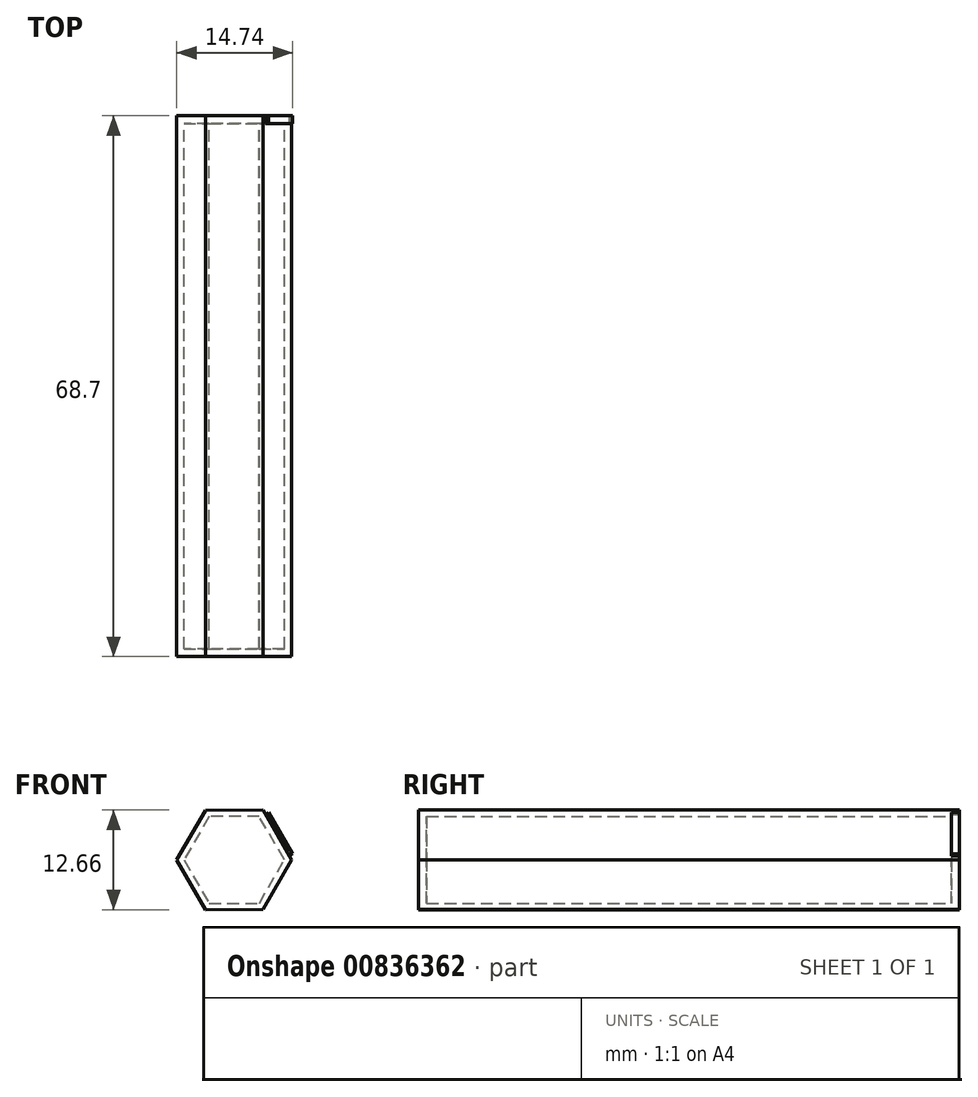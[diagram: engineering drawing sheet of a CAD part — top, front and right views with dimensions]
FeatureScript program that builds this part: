
annotation { "Feature Type Name" : "Feature", "Feature Type Description" : "" }
export const myFeature = defineFeature(function(context is Context, id is Id, definition is map)
    precondition{}
    {
        {
            var Q0;
            Q0=qCreatedBy(makeId("Front.planeOp"),FACE);
            var sketch = newSketch(context, id + "F0", { "sketchPlane" : qUnion([Q0])});
            skLineSegment(sketch, "E0.0", {"start": v(3.64, 6.33) * mm, "end": v(7.3, 0.02) * mm});
            skLineSegment(sketch, "E0.1", {"start": v(7.3, 0.02) * mm, "end": v(3.66, -6.31) * mm});
            skLineSegment(sketch, "E0.2", {"start": v(3.66, -6.31) * mm, "end": v(-3.64, -6.33) * mm});
            skLineSegment(sketch, "E0.3", {"start": v(-3.64, -6.33) * mm, "end": v(-7.3, -0.02) * mm});
            skLineSegment(sketch, "E0.4", {"start": v(-7.3, -0.02) * mm, "end": v(-3.66, 6.31) * mm});
            skLineSegment(sketch, "E0.5", {"start": v(-3.66, 6.31) * mm, "end": v(3.64, 6.33) * mm});
            skPoint(sketch, "E0.0.midPoint", {"position": v(5.47, 3.17) * mm});
            skSolve(sketch);
        }
        {
            var Q0;
            Q0=makeQuery(id+"F0.imprint","IMPRINT",FACE,{"disambiguationData":[TD([[makeQuery(id+"F0.imprint","IMPRINT",EDGE,{"derivedFrom":sQuery(id+"F0.wireOp",EDGE,"E0.0")}),-1.0]])]});
            extrude(context, id + "F1", {"entities" : qUnion([Q0]), "depth" : 69.5 * mm, "offsetDistance" : 25 * mm});
        }
        {
            var Q0;
            Q0=makeQuery(id+"F1.opExtrude","CAP_FACE",FACE,{"disambiguationData":[OSD([sQuery(id+"F0.wireOp",EDGE,"E0.0"),sQuery(id+"F0.wireOp",EDGE,"E0.1"),sQuery(id+"F0.wireOp",EDGE,"E0.2"),sQuery(id+"F0.wireOp",EDGE,"E0.3"),sQuery(id+"F0.wireOp",EDGE,"E0.4"),sQuery(id+"F0.wireOp",EDGE,"E0.5")])],"isStart":true});
            shell(context, id + "F2", {"entities" : qUnion([Q0]), "thickness" : 0.8 * mm});
        }
        {
            var Q0;
            Q0=makeQuery(id+"F1.opExtrude","CAP_FACE",FACE,{"disambiguationData":[OSD([sQuery(id+"F0.wireOp",EDGE,"E0.0"),sQuery(id+"F0.wireOp",EDGE,"E0.1"),sQuery(id+"F0.wireOp",EDGE,"E0.2"),sQuery(id+"F0.wireOp",EDGE,"E0.3"),sQuery(id+"F0.wireOp",EDGE,"E0.4"),sQuery(id+"F0.wireOp",EDGE,"E0.5")])],"isStart":false});
            extrude(context, id + "F3", {"entities" : qUnion([Q0]), "operationType" : NewBodyOperationType.REMOVE, "oppositeDirection" : true, "depth" : 0.8 * mm, "offsetDistance" : 25 * mm});
        }
        {
            var Q0;
            Q0=makeQuery(id+"F3.boolean.opBoolean","COPY",FACE,{"derivedFrom":makeQuery(id+"F3.opExtrude","CAP_FACE",FACE,{"disambiguationData":[OSD([sQuery(id+"F0.wireOp",EDGE,"E0.0"),sQuery(id+"F0.wireOp",EDGE,"E0.1"),sQuery(id+"F0.wireOp",EDGE,"E0.2"),sQuery(id+"F0.wireOp",EDGE,"E0.3"),sQuery(id+"F0.wireOp",EDGE,"E0.4"),sQuery(id+"F0.wireOp",EDGE,"E0.5")])],"isStart":false})});
            var sketch = newSketch(context, id + "F4", { "sketchPlane" : qUnion([Q0])});
            skLineSegment(sketch, "E1", {"start": v(3.18, 5.53) * mm, "end": v(6.38, 0.01) * mm});
            skLineSegment(sketch, "E2", {"start": v(7.3, 0.02) * mm, "end": v(3.64, 6.33) * mm});
            skLineSegment(sketch, "E3", {"start": v(-7.3, -0.02) * mm, "end": v(-3.64, -6.33) * mm});
            skLineSegment(sketch, "E4", {"start": v(-3.18, -5.53) * mm, "end": v(-6.38, -0.01) * mm});
            skLineSegment(sketch, "E5", {"start": v(3.64, 6.33) * mm, "end": v(5.47, 3.17) * mm});
            skLineSegment(sketch, "E6", {"start": v(5.47, 3.17) * mm, "end": v(-5.47, -3.17) * mm});
            skLineSegment(sketch, "E7", {"start": v(-4.78, -2.77) * mm, "end": v(4.78, 2.77) * mm});
            skSolve(sketch);
        }
        {
            var Q0;
            {var subQ3=sQuery(id+"F4.wireOp",EDGE,"E7");Q0=makeQuery(id+"F4.imprint","IMPRINT",FACE,{"disambiguationData":[TD([[makeQuery(id+"F4.imprint","IMPRINT",EDGE,{"derivedFrom":subQ3}),1.0]])]});}
            var sketch = newSketch(context, id + "F5", { "sketchPlane" : qUnion([Q0])});
            skLineSegment(sketch, "E8", {"start": v(-3.2, 5.52) * mm, "end": v(3.18, 5.53) * mm});
            skLineSegment(sketch, "E9", {"start": v(3.18, 5.53) * mm, "end": v(6.38, 0.01) * mm});
            skLineSegment(sketch, "E10", {"start": v(6.38, 0.01) * mm, "end": v(3.2, -5.51) * mm});
            skLineSegment(sketch, "E11", {"start": v(3.2, -5.51) * mm, "end": v(-3.18, -5.53) * mm});
            skLineSegment(sketch, "E12", {"start": v(-3.18, -5.53) * mm, "end": v(-6.38, -0.01) * mm});
            skLineSegment(sketch, "E13", {"start": v(-6.38, -0.01) * mm, "end": v(-3.2, 5.52) * mm});
            skLineSegment(sketch, "E14", {"start": v(-3, 5.52) * mm, "end": v(-3, 5.02) * mm});
            skLineSegment(sketch, "E15", {"start": v(2.3, 5.53) * mm, "end": v(2.3, 5.03) * mm});
            skLineSegment(sketch, "E16", {"start": v(3.7, 4.62) * mm, "end": v(3.27, 4.37) * mm});
            skLineSegment(sketch, "E17", {"start": v(5.9, 0.85) * mm, "end": v(5.46, 0.6) * mm});
            skLineSegment(sketch, "E18", {"start": v(5.86, -0.9) * mm, "end": v(5.42, -0.64) * mm});
            skLineSegment(sketch, "E19", {"start": v(3.7, -4.64) * mm, "end": v(3.27, -4.4) * mm});
            skLineSegment(sketch, "E20", {"start": v(2.49, -5.52) * mm, "end": v(2.49, -5.02) * mm});
            skLineSegment(sketch, "E21", {"start": v(-2.37, -5.53) * mm, "end": v(-2.37, -5.03) * mm});
            skLineSegment(sketch, "E22", {"start": v(-3.8, -4.47) * mm, "end": v(-3.36, -4.22) * mm});
            skLineSegment(sketch, "E23", {"start": v(-5.9, -0.82) * mm, "end": v(-5.47, -0.57) * mm});
            skLineSegment(sketch, "E24", {"start": v(-5.88, 0.85) * mm, "end": v(-5.45, 0.6) * mm});
            skLineSegment(sketch, "E25", {"start": v(-3.8, 4.48) * mm, "end": v(-3.36, 4.23) * mm});
            skLineSegment(sketch, "E26", {"start": v(-3, 5.02) * mm, "end": v(2.3, 5.03) * mm});
            skLineSegment(sketch, "E27", {"start": v(3.27, 4.37) * mm, "end": v(5.46, 0.6) * mm});
            skLineSegment(sketch, "E28", {"start": v(5.42, -0.64) * mm, "end": v(3.27, -4.4) * mm});
            skLineSegment(sketch, "E29", {"start": v(2.49, -5.02) * mm, "end": v(-2.37, -5.03) * mm});
            skLineSegment(sketch, "E30", {"start": v(-3.36, -4.22) * mm, "end": v(-5.47, -0.57) * mm});
            skLineSegment(sketch, "E31", {"start": v(-5.45, 0.6) * mm, "end": v(-2.91, 5.02) * mm});
            skLineSegment(sketch, "E32", {"start": v(2.3, 5.03) * mm, "end": v(3.2, 5.03) * mm});
            skLineSegment(sketch, "E33", {"start": v(3.27, 4.37) * mm, "end": v(2.89, 5.03) * mm});
            skLineSegment(sketch, "E34", {"start": v(5.42, -0.64) * mm, "end": v(5.94, 0.27) * mm});
            skLineSegment(sketch, "E35", {"start": v(5.46, 0.6) * mm, "end": v(5.8, 0) * mm});
            skLineSegment(sketch, "E36", {"start": v(3.27, -4.4) * mm, "end": v(2.83, -5.16) * mm});
            skLineSegment(sketch, "E37", {"start": v(2.49, -5.02) * mm, "end": v(2.91, -5.02) * mm});
            skLineSegment(sketch, "E38", {"start": v(-2.37, -5.03) * mm, "end": v(-3.17, -5.03) * mm});
            skLineSegment(sketch, "E39", {"start": v(-3.36, -4.22) * mm, "end": v(-2.89, -5.03) * mm});
            skLineSegment(sketch, "E40", {"start": v(-5.47, -0.57) * mm, "end": v(-5.94, 0.23) * mm});
            skLineSegment(sketch, "E41", {"start": v(-5.45, 0.6) * mm, "end": v(-5.8, -0.01) * mm});
            skSolve(sketch);
        }
        {
            var Q0;
            Q0=qSketchRegion(id+"F5",true);
            extrude(context, id + "F6", {"entities" : qUnion([Q0]), "operationType" : NewBodyOperationType.ADD, "oppositeDirection" : true, "depth" : 1 * mm, "offsetDistance" : 25 * mm});
        }
        {
            var Q0;
            Q0=makeQuery(id+"F1.opExtrude","CAP_FACE",FACE,{"disambiguationData":[OSD([sQuery(id+"F0.wireOp",EDGE,"E0.0"),sQuery(id+"F0.wireOp",EDGE,"E0.1"),sQuery(id+"F0.wireOp",EDGE,"E0.2"),sQuery(id+"F0.wireOp",EDGE,"E0.3"),sQuery(id+"F0.wireOp",EDGE,"E0.4"),sQuery(id+"F0.wireOp",EDGE,"E0.5")])],"isStart":true});
            var sketch = newSketch(context, id + "F7", { "sketchPlane" : qUnion([Q0])});
            skLineSegment(sketch, "E42.0", {"start": v(3.66, 6.31) * mm, "end": v(7.3, -0.02) * mm});
            skLineSegment(sketch, "E42.1", {"start": v(7.3, -0.02) * mm, "end": v(3.64, -6.33) * mm});
            skLineSegment(sketch, "E42.2", {"start": v(3.64, -6.33) * mm, "end": v(-3.66, -6.31) * mm});
            skLineSegment(sketch, "E42.3", {"start": v(-3.66, -6.31) * mm, "end": v(-7.3, 0.02) * mm});
            skLineSegment(sketch, "E42.4", {"start": v(-7.3, 0.02) * mm, "end": v(-3.64, 6.33) * mm});
            skLineSegment(sketch, "E42.5", {"start": v(-3.64, 6.33) * mm, "end": v(3.66, 6.31) * mm});
            skPoint(sketch, "E42.0.midPoint", {"position": v(5.48, 3.15) * mm});
            skLineSegment(sketch, "E43", {"start": v(-3.3, 6.33) * mm, "end": v(-3.3, 6.83) * mm});
            skLineSegment(sketch, "E44", {"start": v(3.41, 6.31) * mm, "end": v(3.41, 6.81) * mm});
            skLineSegment(sketch, "E45", {"start": v(3.96, 5.8) * mm, "end": v(4.4, 6.05) * mm});
            skLineSegment(sketch, "E46", {"start": v(7, 0.5) * mm, "end": v(7.44, 0.74) * mm});
            skLineSegment(sketch, "E47", {"start": v(7, -0.55) * mm, "end": v(7.42, -0.8) * mm});
            skLineSegment(sketch, "E48", {"start": v(4.18, -5.4) * mm, "end": v(4.61, -5.65) * mm});
            skLineSegment(sketch, "E49", {"start": v(3, -6.33) * mm, "end": v(3, -6.83) * mm});
            skLineSegment(sketch, "E50", {"start": v(-3.12, -6.32) * mm, "end": v(-3.12, -6.82) * mm});
            skLineSegment(sketch, "E51", {"start": v(-3.99, -5.75) * mm, "end": v(-4.42, -6) * mm});
            skLineSegment(sketch, "E52", {"start": v(-6.67, -1.09) * mm, "end": v(-7.1, -1.33) * mm});
            skLineSegment(sketch, "E53", {"start": v(-7.01, 0.51) * mm, "end": v(-7.44, 0.76) * mm});
            skLineSegment(sketch, "E54", {"start": v(-3.96, 5.77) * mm, "end": v(-4.4, 6.02) * mm});
            skLineSegment(sketch, "E55", {"start": v(-3.3, 6.83) * mm, "end": v(3.41, 6.81) * mm});
            skLineSegment(sketch, "E56", {"start": v(4.4, 6.05) * mm, "end": v(8.5, -1.1) * mm});
            skLineSegment(sketch, "E57", {"start": v(7.42, -0.8) * mm, "end": v(3.8, -7.03) * mm});
            skLineSegment(sketch, "E58", {"start": v(3, -6.83) * mm, "end": v(-5.02, -6.81) * mm});
            skLineSegment(sketch, "E59", {"start": v(-4.42, -6) * mm, "end": v(-8.1, 0.4) * mm});
            skLineSegment(sketch, "E60", {"start": v(-7.44, 0.76) * mm, "end": v(-3.69, 7.24) * mm});
            skLineSegment(sketch, "E61", {"start": v(-3.3, 6.83) * mm, "end": v(-3.92, 6.83) * mm});
            skLineSegment(sketch, "E62", {"start": v(4.4, 6.05) * mm, "end": v(3.82, 7.04) * mm});
            skLineSegment(sketch, "E63", {"start": v(3.41, 6.81) * mm, "end": v(3.95, 6.81) * mm});
            skLineSegment(sketch, "E64", {"start": v(7.42, -0.8) * mm, "end": v(7.88, -0.02) * mm});
            skLineSegment(sketch, "E65", {"start": v(3, -6.83) * mm, "end": v(3.92, -6.83) * mm});
            skLineSegment(sketch, "E66", {"start": v(-4.42, -6) * mm, "end": v(-3.95, -6.81) * mm});
            skLineSegment(sketch, "E67", {"start": v(-7.44, 0.76) * mm, "end": v(-7.88, 0.02) * mm});
            skSolve(sketch);
        }
        {
            var Q0;
            Q0=qSketchRegion(id+"F7",true);
            extrude(context, id + "F8", {"entities" : qUnion([Q0]), "operationType" : NewBodyOperationType.ADD, "oppositeDirection" : true, "depth" : 1 * mm, "offsetDistance" : 25 * mm});
        }
    });
